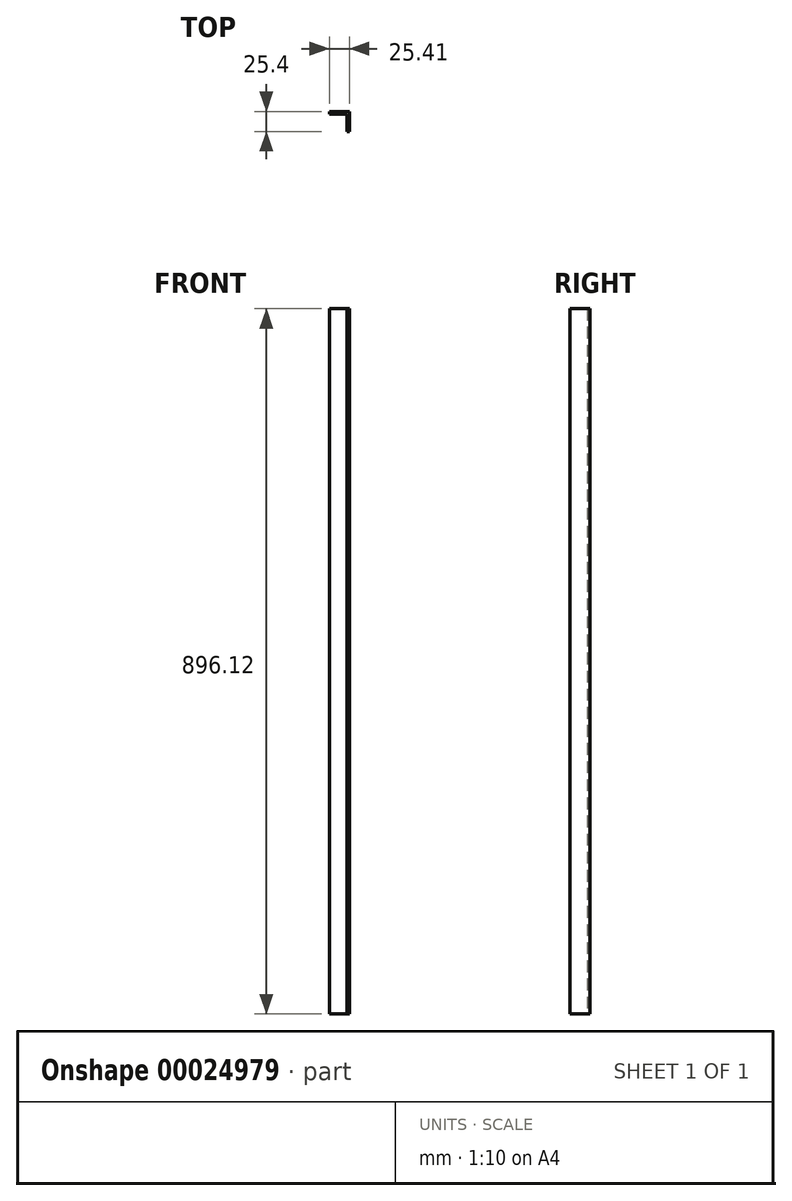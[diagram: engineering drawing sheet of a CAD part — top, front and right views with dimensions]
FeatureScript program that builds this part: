
annotation { "Feature Type Name" : "Feature", "Feature Type Description" : "" }
export const myFeature = defineFeature(function(context is Context, id is Id, definition is map)
    precondition{}
    {
        {
            var Q0;
            Q0=qCreatedBy(makeId("Top.planeOp"),FACE);
            var sketch = newSketch(context, id + "F0", { "sketchPlane" : qUnion([Q0])});
            skLineSegment(sketch, "E0.bottom", {"start": v(-22.23, 9.4) * mm, "end": v(0, 9.4) * mm});
            skLineSegment(sketch, "E0.top", {"start": v(-22.23, 6.22) * mm, "end": v(0, 6.22) * mm});
            skLineSegment(sketch, "E0.left", {"start": v(-22.23, 9.4) * mm, "end": v(-22.23, 6.22) * mm});
            skLineSegment(sketch, "E0.right", {"start": v(0, 9.4) * mm, "end": v(0, 6.22) * mm});
            skLineSegment(sketch, "E1.bottom", {"start": v(0, 9.4) * mm, "end": v(3.18, 9.4) * mm});
            skLineSegment(sketch, "E1.top", {"start": v(0, -16) * mm, "end": v(3.18, -16) * mm});
            skLineSegment(sketch, "E1.left", {"start": v(0, 9.4) * mm, "end": v(0, -16) * mm});
            skLineSegment(sketch, "E1.right", {"start": v(3.17, 9.4) * mm, "end": v(3.18, -16) * mm});
            skSolve(sketch);
        }
        {
            var Q0;
            {var subQ2=sQuery(id+"F0.wireOp",EDGE,"E0.bottom");Q0=makeQuery(id+"F0.imprint","IMPRINT",FACE,{"disambiguationData":[TD([[makeQuery(id+"F0.imprint","IMPRINT",EDGE,{"derivedFrom":subQ2}),-1.0]])]});}
            var Q1;
            {var subQ3=sQuery(id+"F0.wireOp",EDGE,"E1.bottom");Q1=makeQuery(id+"F0.imprint","IMPRINT",FACE,{"disambiguationData":[TD([[makeQuery(id+"F0.imprint","IMPRINT",EDGE,{"derivedFrom":subQ3}),-1.0]])]});}
            extrude(context, id + "F1", {"entities" : qUnion([Q0, Q1]), "depth" : 896.12 * mm});
        }
    });
